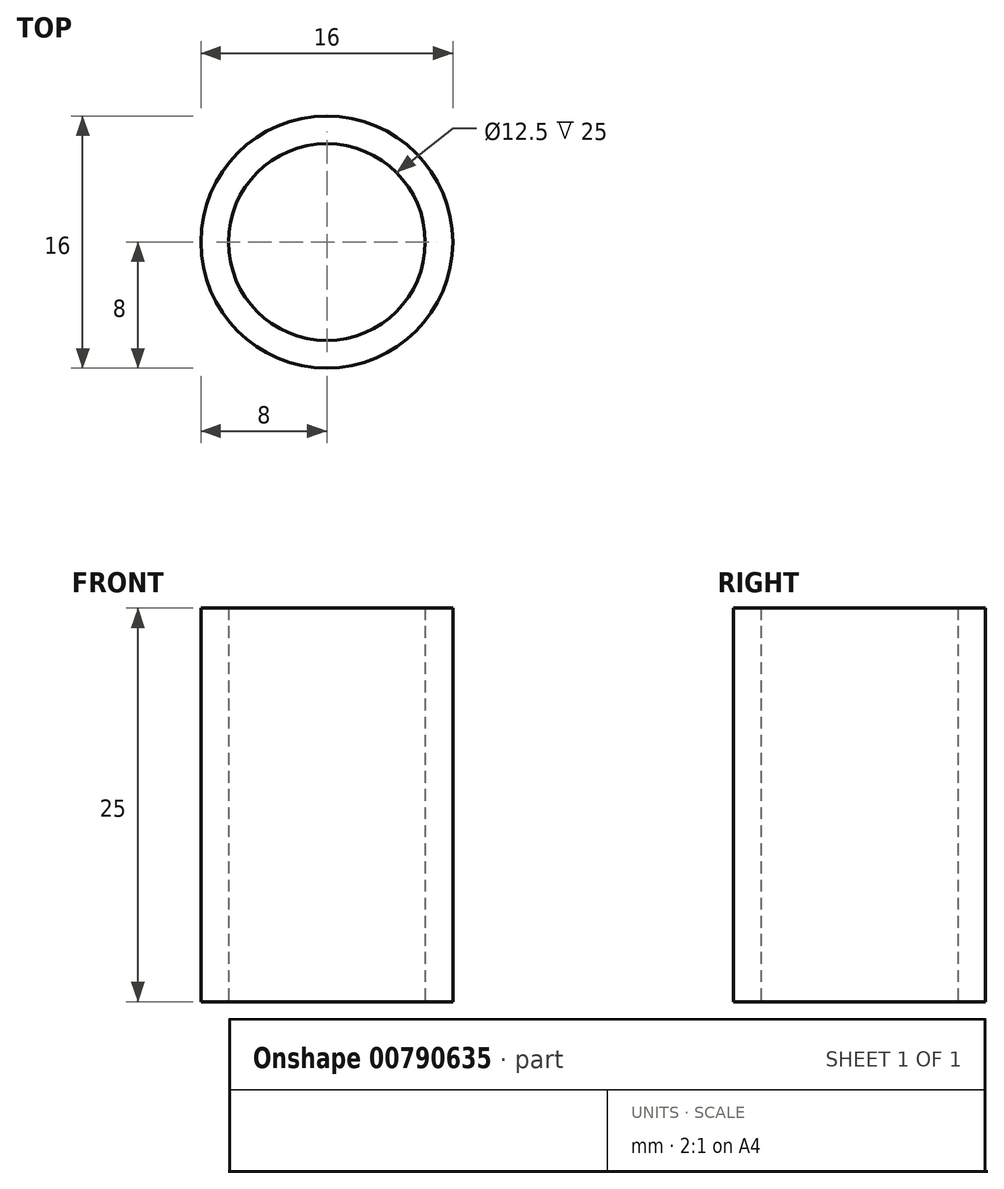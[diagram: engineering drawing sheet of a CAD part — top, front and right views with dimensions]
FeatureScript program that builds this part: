
annotation { "Feature Type Name" : "Feature", "Feature Type Description" : "" }
export const myFeature = defineFeature(function(context is Context, id is Id, definition is map)
    precondition{}
    {
        {
            var Q0;
            Q0=qCreatedBy(makeId("Top.planeOp"),FACE);
            var sketch = newSketch(context, id + "F0", { "sketchPlane" : qUnion([Q0])});
            skCircle(sketch, "E0", {"center": v(0, 0) * mm, "radius": 6.25 * mm});
            skCircle(sketch, "E1", {"center": v(0, 0) * mm, "radius": 8 * mm});
            skSolve(sketch);
        }
        {
            var Q0;
            Q0 = qSketchRegion(id + "F0", true);
            extrude(context, id + "F1", {"entities" : qUnion([Q0]), "depth" : 25 * mm, "offsetDistance" : 25 * mm});
        }
    });
